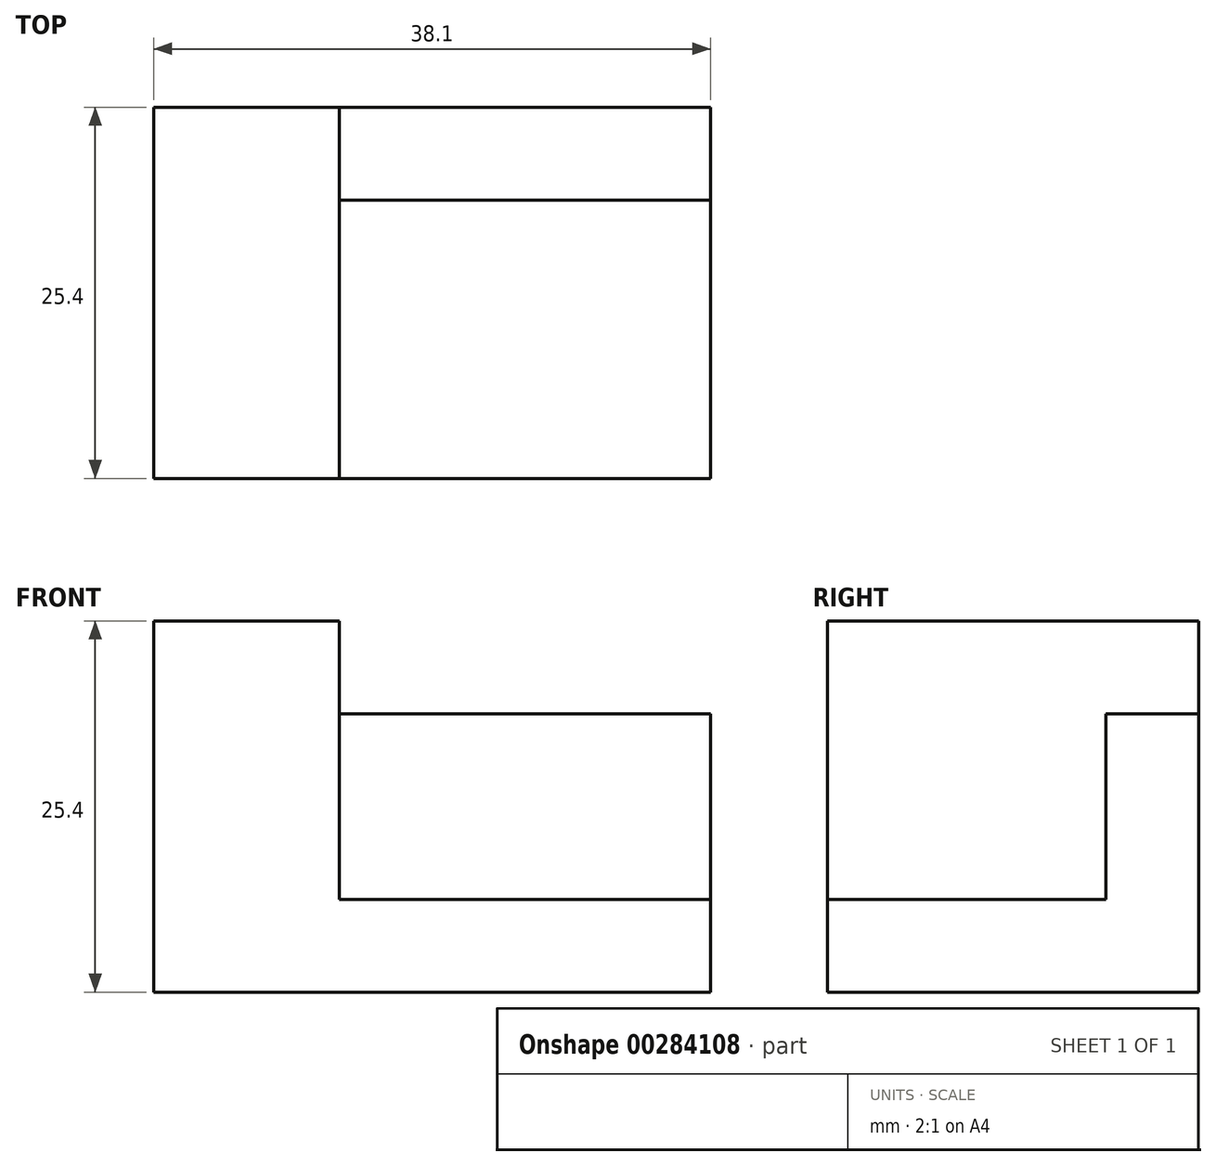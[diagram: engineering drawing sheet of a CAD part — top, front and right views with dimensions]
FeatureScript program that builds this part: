
annotation { "Feature Type Name" : "Feature", "Feature Type Description" : "" }
export const myFeature = defineFeature(function(context is Context, id is Id, definition is map)
    precondition{}
    {
        {
            var Q0;
            Q0=qCreatedBy(makeId("Top.planeOp"),FACE);
            var sketch = newSketch(context, id + "F0", { "sketchPlane" : qUnion([Q0])});
            skLineSegment(sketch, "E0.bottom", {"start": v(0, 0) * mm, "end": v(38.1, 0) * mm});
            skLineSegment(sketch, "E0.top", {"start": v(0, -25.4) * mm, "end": v(38.1, -25.4) * mm});
            skLineSegment(sketch, "E0.left", {"start": v(0, 0) * mm, "end": v(0, -25.4) * mm});
            skLineSegment(sketch, "E0.right", {"start": v(38.1, 0) * mm, "end": v(38.1, -25.4) * mm});
            skSolve(sketch);
        }
        {
            var Q0;
            Q0=makeQuery(id+"F0.imprint","IMPRINT",FACE,{"disambiguationData":[TD([[makeQuery(id+"F0.imprint","IMPRINT",EDGE,{"derivedFrom":sQuery(id+"F0.wireOp",EDGE,"E0.bottom")}),-1.0]])]});
            extrude(context, id + "F1", {"entities" : qUnion([Q0]), "depth" : 6.35 * mm});
        }
        {
            var Q0;
            Q0=makeQuery(id+"F1.opExtrude","CAP_FACE",FACE,{"disambiguationData":[OSD([sQuery(id+"F0.wireOp",EDGE,"E0.bottom"),sQuery(id+"F0.wireOp",EDGE,"E0.top"),sQuery(id+"F0.wireOp",EDGE,"E0.left"),sQuery(id+"F0.wireOp",EDGE,"E0.right")])],"isStart":false});
            var sketch = newSketch(context, id + "F2", { "sketchPlane" : qUnion([Q0])});
            skLineSegment(sketch, "E1.bottom", {"start": v(0, -25.4) * mm, "end": v(12.7, -25.4) * mm});
            skLineSegment(sketch, "E1.top", {"start": v(0, 0) * mm, "end": v(12.7, 0) * mm});
            skLineSegment(sketch, "E1.left", {"start": v(0, -25.4) * mm, "end": v(0, 0) * mm});
            skLineSegment(sketch, "E1.right", {"start": v(12.7, -25.4) * mm, "end": v(12.7, 0) * mm});
            skSolve(sketch);
        }
        {
            var Q0;
            Q0=makeQuery(id+"F2.imprint","IMPRINT",FACE,{"disambiguationData":[TD([[makeQuery(id+"F2.imprint","IMPRINT",EDGE,{"derivedFrom":sQuery(id+"F2.wireOp",EDGE,"E1.bottom")}),1.0]])]});
            extrude(context, id + "F3", {"entities" : qUnion([Q0]), "operationType" : NewBodyOperationType.ADD, "depth" : 19.05 * mm});
        }
        {
            var Q0;
            Q0=makeQuery(id+"F1.opExtrude","CAP_FACE",FACE,{"disambiguationData":[OSD([sQuery(id+"F0.wireOp",EDGE,"E0.bottom"),sQuery(id+"F0.wireOp",EDGE,"E0.top"),sQuery(id+"F0.wireOp",EDGE,"E0.left"),sQuery(id+"F0.wireOp",EDGE,"E0.right")])],"isStart":false});
            var sketch = newSketch(context, id + "F4", { "sketchPlane" : qUnion([Q0])});
            skLineSegment(sketch, "E2.bottom", {"start": v(12.7, 0) * mm, "end": v(38.1, 0) * mm});
            skLineSegment(sketch, "E2.top", {"start": v(12.7, -6.35) * mm, "end": v(38.1, -6.35) * mm});
            skLineSegment(sketch, "E2.left", {"start": v(12.7, 0) * mm, "end": v(12.7, -6.35) * mm});
            skLineSegment(sketch, "E2.right", {"start": v(38.1, 0) * mm, "end": v(38.1, -6.35) * mm});
            skSolve(sketch);
        }
        {
            var Q0;
            Q0 = qSketchRegion(id + "F4", true);
            extrude(context, id + "F5", {"entities" : qUnion([Q0]), "operationType" : NewBodyOperationType.ADD, "depth" : 12.7 * mm});
        }
    });
